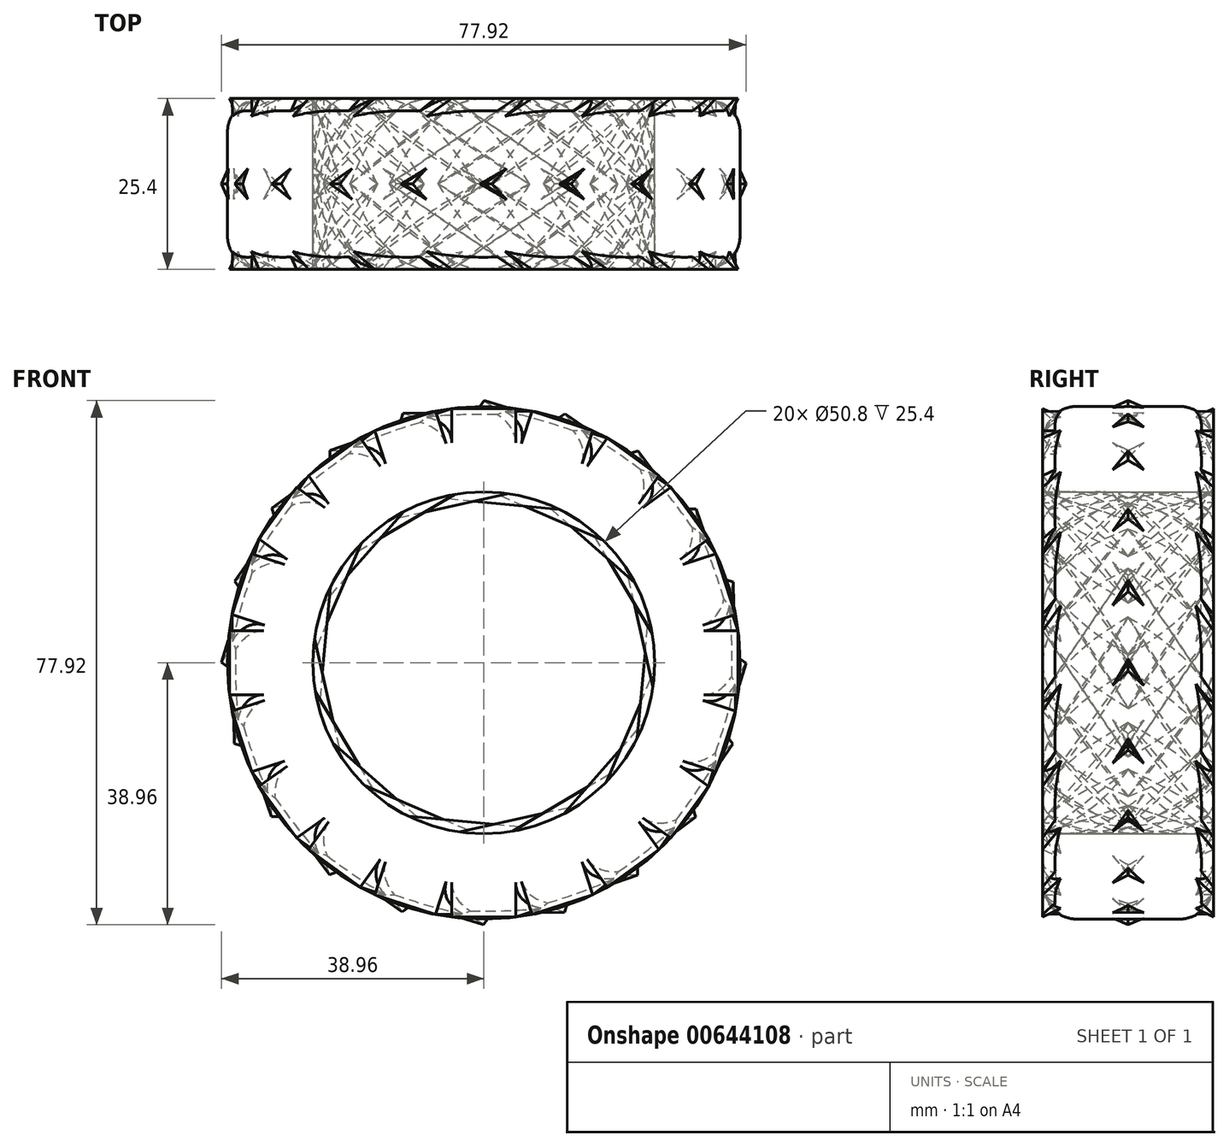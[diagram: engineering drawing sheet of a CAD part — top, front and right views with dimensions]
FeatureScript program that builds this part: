
annotation { "Feature Type Name" : "Feature", "Feature Type Description" : "" }
export const myFeature = defineFeature(function(context is Context, id is Id, definition is map)
    precondition{}
    {
        {
            var Q0;
            Q0=qCreatedBy(makeId("Front.planeOp"),FACE);
            var sketch = newSketch(context, id + "F0", { "sketchPlane" : qUnion([Q0])});
            skCircle(sketch, "E0", {"center": v(0, 0) * mm, "radius": 25.4 * mm});
            skCircle(sketch, "E1", {"center": v(0, 0) * mm, "radius": 38.1 * mm});
            skSolve(sketch);
        }
        {
            var Q0;
            Q0 = qSketchRegion(id + "F0", true);
            extrude(context, id + "F1", {"entities" : qUnion([Q0]), "endBound" : BoundingType.SYMMETRIC, "depth" : 25.4 * mm, "offsetDistance" : 25.4 * mm});
        }
        {
            var Q0;
            Q0=makeQuery(id+"F1.opExtrude","CAP_EDGE",EDGE,{"disambiguationData":[OSD([sQuery(id+"F0.wireOp",EDGE,"E1")])],"isStart":false});
            var Q1;
            Q1=makeQuery(id+"F1.opExtrude","CAP_EDGE",EDGE,{"disambiguationData":[OSD([sQuery(id+"F0.wireOp",EDGE,"E1")])],"isStart":true});
            fillet(context, id + "F2", {"entities" : qUnion([Q0, Q1]), "radius" : 5.08 * mm, "tangentPropagation" : true, "allowEdgeOverflow" : false});
        }
        {
            var Q0;
            Q0=makeQuery(id+"F1.opExtrude","CAP_FACE",FACE,{"disambiguationData":[OSD([sQuery(id+"F0.wireOp",EDGE,"E0"),sQuery(id+"F0.wireOp",EDGE,"E1")])],"isStart":false});
            var sketch = newSketch(context, id + "F3", { "sketchPlane" : qUnion([Q0])});
            skLineSegment(sketch, "E2.bottom", {"start": v(-4.75, 37.8) * mm, "end": v(4.75, 37.8) * mm});
            skLineSegment(sketch, "E2.top", {"start": v(-4.75, 25.4) * mm, "end": v(4.75, 25.4) * mm});
            skLineSegment(sketch, "E2.left", {"start": v(-4.75, 37.8) * mm, "end": v(-4.75, 25.4) * mm});
            skLineSegment(sketch, "E2.right", {"start": v(4.75, 37.8) * mm, "end": v(4.75, 25.4) * mm});
            skSolve(sketch);
        }
        {
            var Q0;
            Q0=qCreatedBy(makeId("Front.planeOp"),FACE);
            var sketch = newSketch(context, id + "F4", { "sketchPlane" : qUnion([Q0])});
            skLineSegment(sketch, "E3.bottom", {"start": v(-22.85, 31.55) * mm, "end": v(-14, 31.55) * mm});
            skLineSegment(sketch, "E3.top", {"start": v(-22.85, 21.19) * mm, "end": v(-14, 21.19) * mm});
            skLineSegment(sketch, "E3.left", {"start": v(-22.85, 31.55) * mm, "end": v(-22.85, 21.19) * mm});
            skLineSegment(sketch, "E3.right", {"start": v(-14, 31.55) * mm, "end": v(-14, 21.19) * mm});
            skSolve(sketch);
        }
        {
            var Q1;
            Q1 = qSketchRegion(id + "F3", true);
            var Q2;
            Q2 = qSketchRegion(id + "F4", true);
            loft(context, id + "F5", {"operationType" : NewBodyOperationType.ADD, "sheetProfilesArray" : [{ "sheetProfileEntities" : qUnion([Q1]) }, { "sheetProfileEntities" : qUnion([Q2]) }]});
        }
        {
            var Q0;
            Q0=makeQuery(id+"F1.opExtrude","SWEPT_BODY",BODY,{"disambiguationData":[OSD([sQuery(id+"F0.wireOp",EDGE,"E0"),sQuery(id+"F0.wireOp",EDGE,"E1")])]});
            var Q1;
            Q1=qCreatedBy(makeId("Front.planeOp"),FACE);
            mirror(context, id + "F6", {"operationType" : NewBodyOperationType.ADD, "entities" : qUnion([Q0]), "mirrorPlane" : qUnion([Q1])});
        }
        {
            var Q0;
            Q0=makeQuery(id+"F1.opExtrude","SWEPT_BODY",BODY,{"disambiguationData":[OSD([sQuery(id+"F0.wireOp",EDGE,"E0"),sQuery(id+"F0.wireOp",EDGE,"E1")])]});
            var Q1;
            {var subQ0=sQuery(id+"F0.wireOp",EDGE,"E1");Q1=makeQuery(id+"F2.opFillet","BLEND_FACE",FACE,{"disambiguationData":[OSD([subQ0]),TDD([makeQuery(id+"F1.opExtrude","CAP_EDGE",EDGE,{"disambiguationData":[OSD([subQ0])],"isStart":false})])]});}
            circularPattern(context, id + "F7", {"entities" : qUnion([Q0]), "axis" : qUnion([Q1]), "angle" : 360 * degree, "instanceCount" : 20, "equalSpace" : true});
        }
    });
